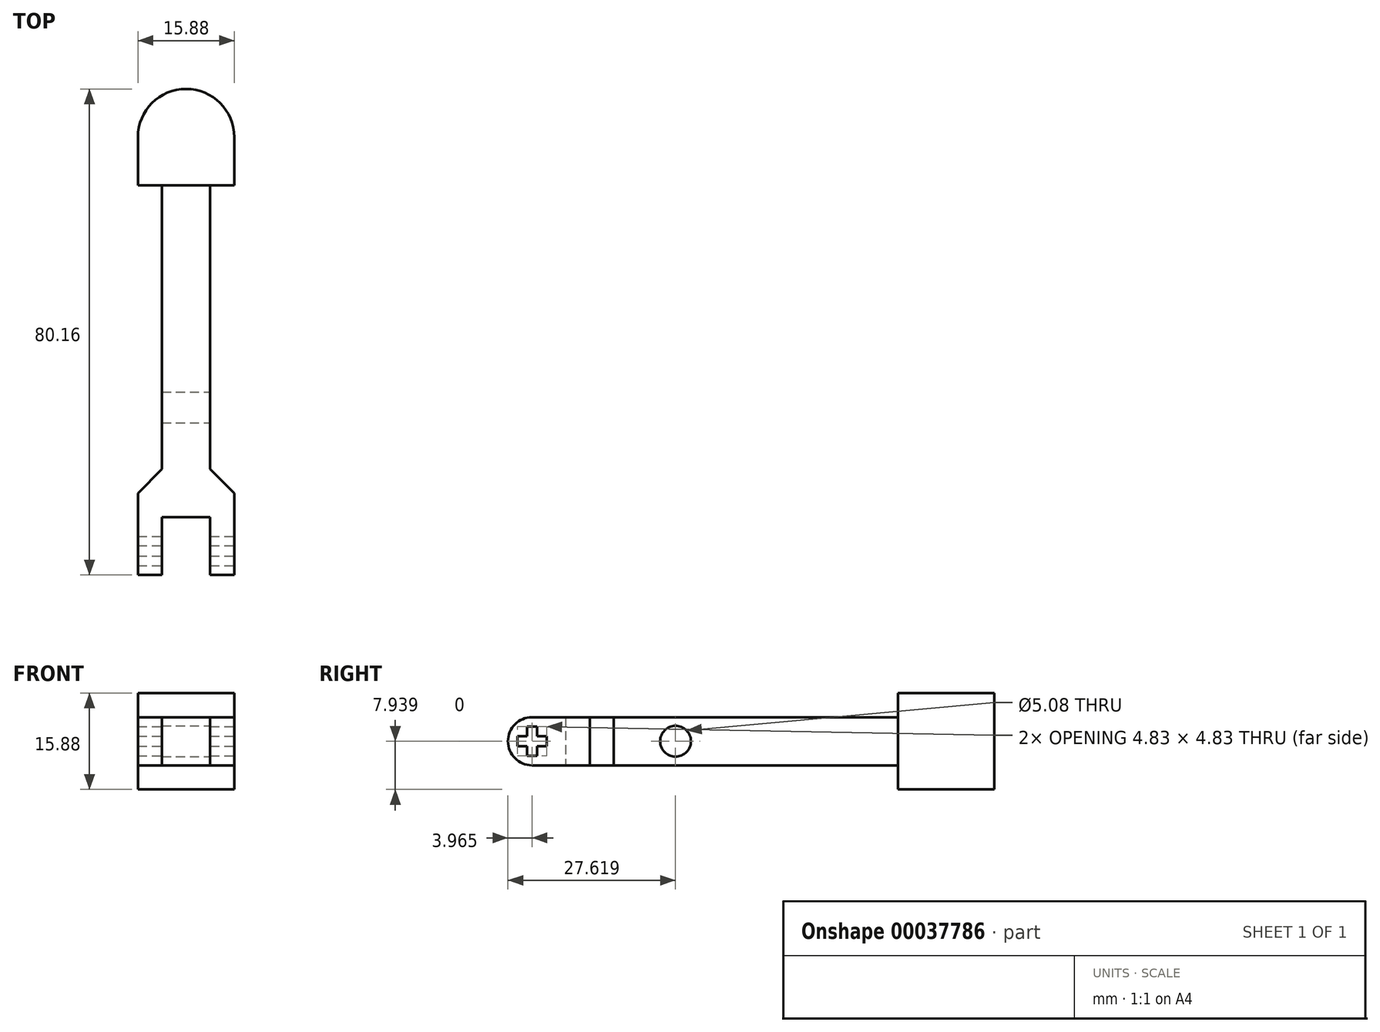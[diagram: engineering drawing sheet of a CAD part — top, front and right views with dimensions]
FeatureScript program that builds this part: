
annotation { "Feature Type Name" : "Feature", "Feature Type Description" : "" }
export const myFeature = defineFeature(function(context is Context, id is Id, definition is map)
    precondition{}
    {
        {
            var Q0;
            Q0=qCreatedBy(makeId("Top.planeOp"),FACE);
            var sketch = newSketch(context, id + "F0", { "sketchPlane" : qUnion([Q0])});
            skLineSegment(sketch, "E0.left", {"start": v(0, 0) * mm, "end": v(0, -13.5) * mm});
            skLineSegment(sketch, "E0.right", {"start": v(15.87, 0) * mm, "end": v(15.87, -13.5) * mm});
            skLineSegment(sketch, "E1", {"start": v(0, -13.5) * mm, "end": v(3.97, -13.5) * mm});
            skLineSegment(sketch, "E2", {"start": v(15.87, -13.5) * mm, "end": v(11.9, -13.5) * mm});
            skLineSegment(sketch, "E3.top", {"start": v(3.97, -3.97) * mm, "end": v(11.9, -3.97) * mm});
            skLineSegment(sketch, "E3.left", {"start": v(3.97, -13.5) * mm, "end": v(3.97, -3.97) * mm});
            skLineSegment(sketch, "E3.right", {"start": v(11.9, -13.5) * mm, "end": v(11.9, -3.97) * mm});
            skLineSegment(sketch, "E4", {"start": v(0, 0) * mm, "end": v(3.97, 0) * mm});
            skLineSegment(sketch, "E5", {"start": v(15.87, 0) * mm, "end": v(11.9, 0) * mm});
            skLineSegment(sketch, "E6", {"start": v(11.9, 0) * mm, "end": v(11.9, 50.8) * mm});
            skLineSegment(sketch, "E7", {"start": v(11.9, 50.8) * mm, "end": v(3.97, 50.8) * mm});
            skLineSegment(sketch, "E8", {"start": v(3.97, 50.8) * mm, "end": v(3.97, 0) * mm});
            skLineSegment(sketch, "E9", {"start": v(11.9, -3.97) * mm, "end": v(11.9, 0) * mm, "construction": true});
            skSolve(sketch);
        }
        {
            var Q0;
            Q0 = qSketchRegion(id + "F0", true);
            extrude(context, id + "F1", {"entities" : qUnion([Q0]), "depth" : 7.94 * mm});
        }
        {
            var Q0;
            Q0=makeQuery(id+"F1.opExtrude","SWEPT_FACE",FACE,{"disambiguationData":[OSD([sQuery(id+"F0.wireOp",EDGE,"E0.right")])]});
            var sketch = newSketch(context, id + "F2", { "sketchPlane" : qUnion([Q0])});
            skLineSegment(sketch, "E10", {"start": v(-3.97, 7.94) * mm, "end": v(-9.52, 7.94) * mm});
            skLineSegment(sketch, "E11", {"start": v(-9.52, 0) * mm, "end": v(-3.97, 0) * mm});
            skArc(sketch, "E12", {"start": v(-9.52, 7.94) * mm, "mid": v(-13.5, 3.97) * mm, "end": v(-9.52, 0) * mm});
            skLineSegment(sketch, "E13.bottom", {"start": v(-3.97, 7.94) * mm, "end": v(-13.5, 7.94) * mm});
            skLineSegment(sketch, "E13.top", {"start": v(-3.97, 0) * mm, "end": v(-13.5, 0) * mm});
            skLineSegment(sketch, "E13.right", {"start": v(-13.5, 7.94) * mm, "end": v(-13.5, 0) * mm});
            skLineSegment(sketch, "E14", {"start": v(-9.52, 3.97) * mm, "end": v(14.13, 3.97) * mm, "construction": true});
            skCircle(sketch, "E15", {"center": v(14.13, 3.97) * mm, "radius": 2.54 * mm});
            skLineSegment(sketch, "E16.rect.bottom", {"start": v(-10.37, 6.38) * mm, "end": v(-8.68, 6.38) * mm});
            skLineSegment(sketch, "E16.rect.top", {"start": v(-10.37, 1.56) * mm, "end": v(-8.68, 1.56) * mm});
            skLineSegment(sketch, "E16.rect.left", {"start": v(-10.37, 6.38) * mm, "end": v(-10.37, 1.56) * mm});
            skLineSegment(sketch, "E16.rect.right", {"start": v(-8.68, 6.38) * mm, "end": v(-8.68, 1.56) * mm});
            skLineSegment(sketch, "E17.rect.bottom", {"start": v(-7.11, 4.81) * mm, "end": v(-11.94, 4.81) * mm});
            skLineSegment(sketch, "E17.rect.top", {"start": v(-7.11, 3.12) * mm, "end": v(-11.94, 3.12) * mm});
            skLineSegment(sketch, "E17.rect.left", {"start": v(-7.11, 4.81) * mm, "end": v(-7.11, 3.12) * mm});
            skLineSegment(sketch, "E17.rect.right", {"start": v(-11.94, 4.81) * mm, "end": v(-11.94, 3.12) * mm});
            skSolve(sketch);
        }
        {
            var Q0;
            Q0 = qSketchRegion(id + "F2", true);
            var Q1;
            Q1=makeQuery(id+"F1.opExtrude","SWEPT_FACE",FACE,{"disambiguationData":[OSD([sQuery(id+"F0.wireOp",EDGE,"E0.left")])]});
            extrude(context, id + "F3", {"entities" : qUnion([Q0]), "operationType" : NewBodyOperationType.REMOVE, "endBound" : BoundingType.UP_TO_SURFACE, "oppositeDirection" : true, "endBoundEntityFace" : qUnion([Q1]), "depth" : 25.4 * mm});
        }
        {
            var Q0;
            Q0=makeQuery(id+"F1.opExtrude","SWEPT_EDGE",EDGE,{"disambiguationData":[OSD([sQuery(id+"F0.wireOp",EDGE,"E5"),sQuery(id+"F0.wireOp",EDGE,"E6")])]});
            var Q1;
            Q1=makeQuery(id+"F1.opExtrude","SWEPT_EDGE",EDGE,{"disambiguationData":[OSD([sQuery(id+"F0.wireOp",EDGE,"E4"),sQuery(id+"F0.wireOp",EDGE,"E8")])]});
            chamfer(context, id + "F4", {"entities" : qUnion([Q0, Q1]), "width" : 3.97 * mm, "tangentPropagation" : true});
        }
        {
            var Q0;
            Q0=makeQuery(id+"F1.opExtrude","SWEPT_FACE",FACE,{"disambiguationData":[OSD([sQuery(id+"F0.wireOp",EDGE,"E7")])]});
            var sketch = newSketch(context, id + "F5", { "sketchPlane" : qUnion([Q0])});
            skLineSegment(sketch, "E18", {"start": v(-7.94, 7.94) * mm, "end": v(-7.94, 0) * mm, "construction": true});
            skLineSegment(sketch, "E19.rect.bottom", {"start": v(0, -3.97) * mm, "end": v(-15.87, -3.97) * mm});
            skLineSegment(sketch, "E19.rect.top", {"start": v(0, 11.9) * mm, "end": v(-15.87, 11.9) * mm});
            skLineSegment(sketch, "E19.rect.left", {"start": v(0, -3.97) * mm, "end": v(0, 11.9) * mm});
            skLineSegment(sketch, "E19.rect.right", {"start": v(-15.87, -3.97) * mm, "end": v(-15.87, 11.9) * mm});
            skPoint(sketch, "E19.rect.middle", {"position": v(-7.94, 3.97) * mm});
            skSolve(sketch);
        }
        {
            var Q0;
            Q0 = qSketchRegion(id + "F5", true);
            extrude(context, id + "F6", {"entities" : qUnion([Q0]), "operationType" : NewBodyOperationType.ADD, "depth" : 15.88 * mm});
        }
        {
            var Q0;
            Q0=makeQuery(id+"F6.opExtrude","CAP_EDGE",EDGE,{"disambiguationData":[OSD([sQuery(id+"F5.wireOp",EDGE,"E19.rect.right")])],"isStart":false});
            var Q1;
            Q1=makeQuery(id+"F6.opExtrude","CAP_EDGE",EDGE,{"disambiguationData":[OSD([sQuery(id+"F5.wireOp",EDGE,"E19.rect.left")])],"isStart":false});
            fillet(context, id + "F7", {"entities" : qUnion([Q0, Q1]), "radius" : 7.94 * mm, "tangentPropagation" : true, "allowEdgeOverflow" : false});
        }
    });
